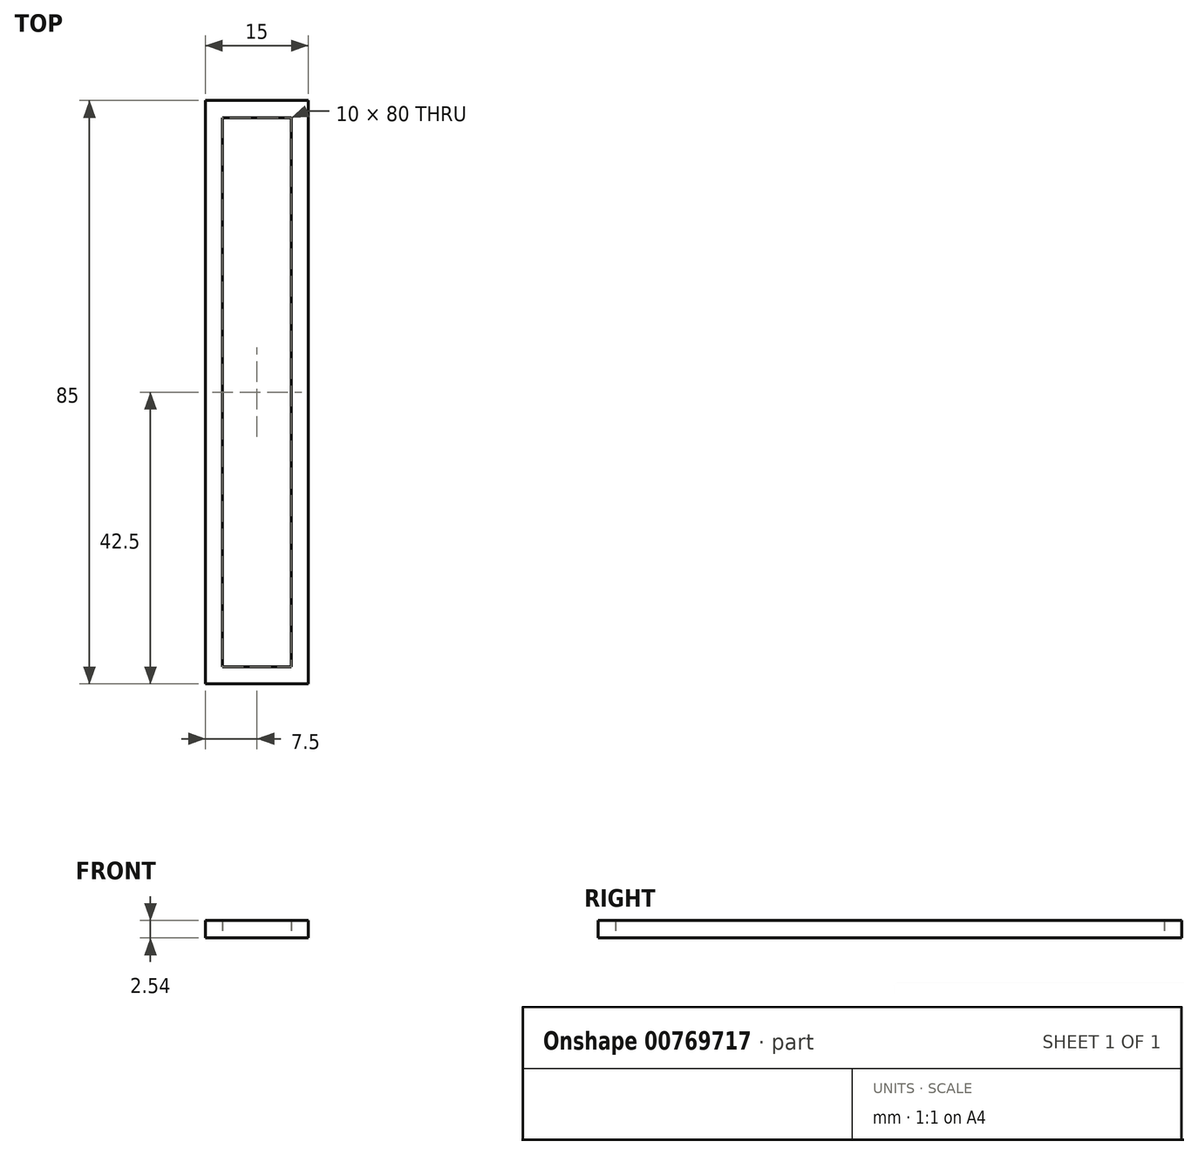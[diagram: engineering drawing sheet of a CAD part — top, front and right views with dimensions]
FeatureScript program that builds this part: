
annotation { "Feature Type Name" : "Feature", "Feature Type Description" : "" }
export const myFeature = defineFeature(function(context is Context, id is Id, definition is map)
    precondition{}
    {
        {
            var Q0;
            Q0=qCreatedBy(makeId("Top.planeOp"),FACE);
            var sketch = newSketch(context, id + "F0", { "sketchPlane" : qUnion([Q0])});
            skLineSegment(sketch, "E0.bottom", {"start": v(7.5, 42.5) * mm, "end": v(-7.5, 42.5) * mm});
            skLineSegment(sketch, "E0.top", {"start": v(7.5, -42.5) * mm, "end": v(-7.5, -42.5) * mm});
            skLineSegment(sketch, "E0.left", {"start": v(7.5, 42.5) * mm, "end": v(7.5, -42.5) * mm});
            skLineSegment(sketch, "E0.right", {"start": v(-7.5, 42.5) * mm, "end": v(-7.5, -42.5) * mm});
            skPoint(sketch, "E0.middle", {"position": v(0, 0) * mm});
            skSolve(sketch);
        }
        {
            var Q0;
            Q0=makeQuery(id+"F0.imprint","IMPRINT",FACE,{"disambiguationData":[TD([[makeQuery(id+"F0.imprint","IMPRINT",EDGE,{"derivedFrom":sQuery(id+"F0.wireOp",EDGE,"E0.bottom")}),1.0]])]});
            extrude(context, id + "F1", {"entities" : qUnion([Q0]), "depth" : 2.54 * mm, "offsetDistance" : 25.4 * mm});
        }
        {
            var Q0;
            Q0=qCreatedBy(makeId("Top.planeOp"),FACE);
            var sketch = newSketch(context, id + "F2", { "sketchPlane" : qUnion([Q0])});
            skLineSegment(sketch, "E1.bottom", {"start": v(5, -40) * mm, "end": v(-5, -40) * mm});
            skLineSegment(sketch, "E1.top", {"start": v(5, 40) * mm, "end": v(-5, 40) * mm});
            skLineSegment(sketch, "E1.left", {"start": v(5, -40) * mm, "end": v(5, 40) * mm});
            skLineSegment(sketch, "E1.right", {"start": v(-5, -40) * mm, "end": v(-5, 40) * mm});
            skPoint(sketch, "E1.middle", {"position": v(0, 0) * mm});
            skSolve(sketch);
        }
        {
            var Q0;
            Q0 = qSketchRegion(id + "F2", true);
            extrude(context, id + "F3", {"entities" : qUnion([Q0]), "operationType" : NewBodyOperationType.REMOVE, "endBound" : BoundingType.THROUGH_ALL, "depth" : 25.4 * mm, "offsetDistance" : 25.4 * mm});
        }
    });
